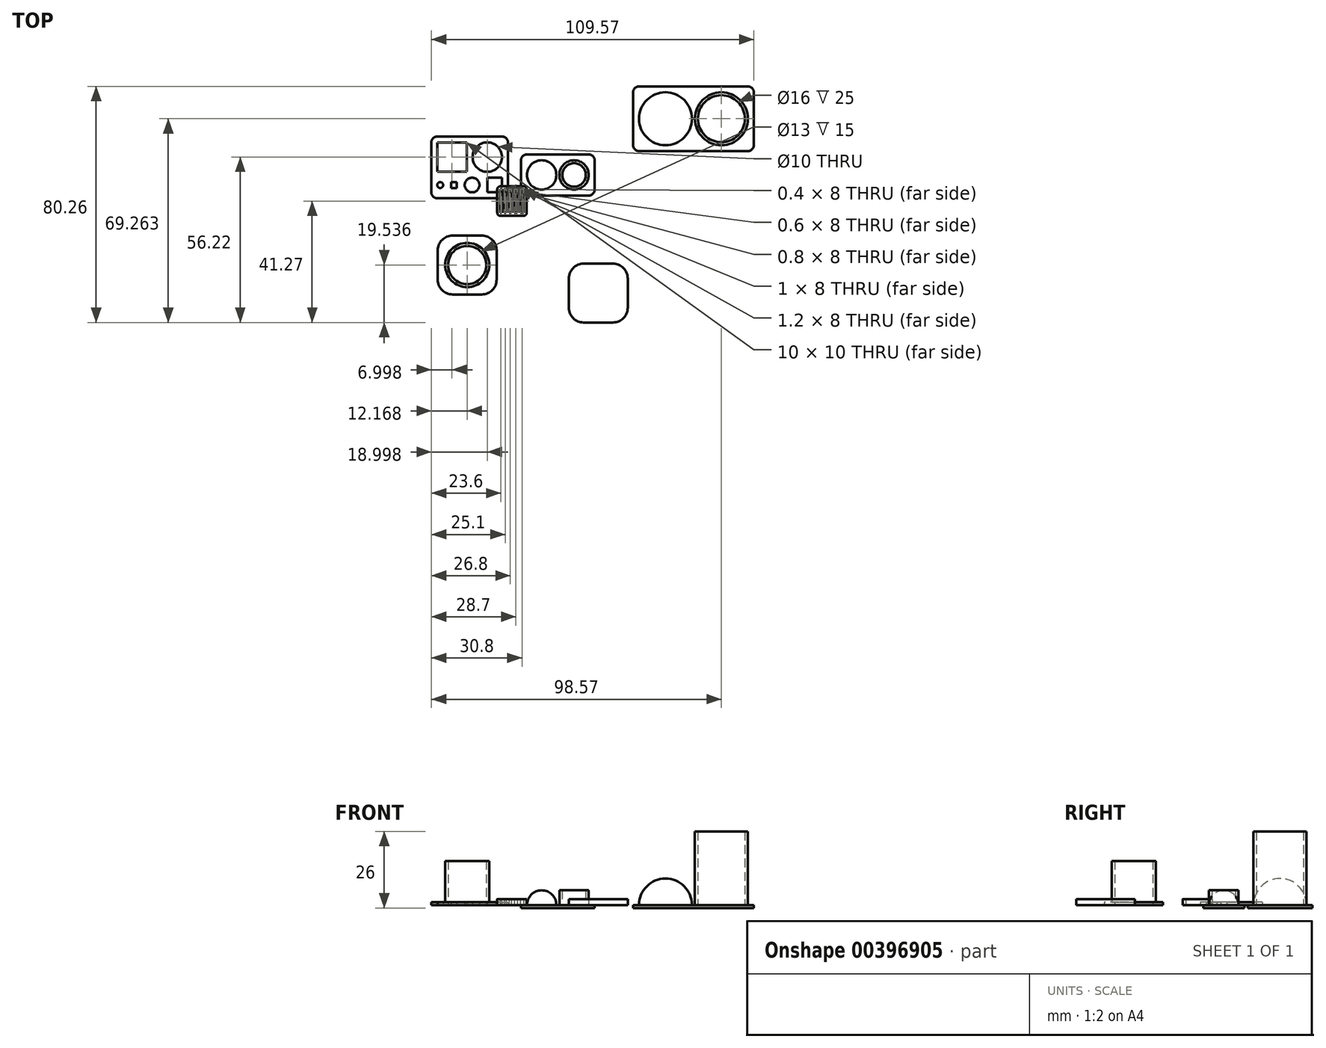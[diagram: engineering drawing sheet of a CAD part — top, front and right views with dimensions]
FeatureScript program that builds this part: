
annotation { "Feature Type Name" : "Feature", "Feature Type Description" : "" }
export const myFeature = defineFeature(function(context is Context, id is Id, definition is map)
    precondition{}
    {
        {
            var Q0;
            Q0=qCreatedBy(makeId("Top.planeOp"),FACE);
            var sketch = newSketch(context, id + "F0", { "sketchPlane" : qUnion([Q0])});
            skCircle(sketch, "E0", {"center": v(21.09, 8.88) * mm, "radius": 4 * mm});
            skCircle(sketch, "E1.0", {"center": v(21.09, 8.88) * mm, "radius": 5 * mm});
            skLineSegment(sketch, "E2", {"start": v(5.09, 8.88) * mm, "end": v(15.09, 8.88) * mm});
            skArc(sketch, "E3", {"start": v(15.09, 8.88) * mm, "mid": v(10.09, 13.88) * mm, "end": v(5.09, 8.88) * mm});
            skLineSegment(sketch, "E4.bottom", {"start": v(5.09, 15.88) * mm, "end": v(26.09, 15.88) * mm});
            skLineSegment(sketch, "E4.top", {"start": v(5.09, 1.88) * mm, "end": v(26.09, 1.88) * mm});
            skLineSegment(sketch, "E4.left", {"start": v(3.09, 13.88) * mm, "end": v(3.09, 3.88) * mm});
            skLineSegment(sketch, "E4.right", {"start": v(28.09, 13.88) * mm, "end": v(28.09, 3.88) * mm});
            skLineSegment(sketch, "E5", {"start": v(5.09, 8.88) * mm, "end": v(5.09, 15.88) * mm, "construction": true});
            skLineSegment(sketch, "E6", {"start": v(5.09, 8.88) * mm, "end": v(5.09, 1.88) * mm, "construction": true});
            skArc(sketch, "E7", {"start": v(5.09, 8.88) * mm, "mid": v(10.09, 3.88) * mm, "end": v(15.09, 8.88) * mm});
            skPoint(sketch, "E8.visualSharp", {"position": v(3.09, 15.88) * mm});
            skArc(sketch, "E8.filletArc", {"start": v(5.09, 15.88) * mm, "mid": v(3.67, 15.3) * mm, "end": v(3.09, 13.88) * mm});
            skPoint(sketch, "E9.visualSharp", {"position": v(3.09, 1.88) * mm});
            skArc(sketch, "E9.filletArc", {"start": v(3.09, 3.88) * mm, "mid": v(3.67, 2.46) * mm, "end": v(5.09, 1.88) * mm});
            skPoint(sketch, "E10.visualSharp", {"position": v(28.09, 1.88) * mm});
            skArc(sketch, "E10.filletArc", {"start": v(26.09, 1.88) * mm, "mid": v(27.5, 2.46) * mm, "end": v(28.09, 3.88) * mm});
            skPoint(sketch, "E11.visualSharp", {"position": v(28.09, 15.88) * mm});
            skArc(sketch, "E11.filletArc", {"start": v(28.09, 13.88) * mm, "mid": v(27.5, 15.3) * mm, "end": v(26.09, 15.88) * mm});
            skCircle(sketch, "E12", {"center": v(71.17, 28) * mm, "radius": 8 * mm});
            skCircle(sketch, "E13.0", {"center": v(71.17, 28) * mm, "radius": 9 * mm});
            skLineSegment(sketch, "E14", {"start": v(43.17, 28) * mm, "end": v(61.17, 28) * mm});
            skArc(sketch, "E15", {"start": v(61.17, 28) * mm, "mid": v(52.17, 37) * mm, "end": v(43.17, 28) * mm});
            skLineSegment(sketch, "E16.bottom", {"start": v(43.17, 39) * mm, "end": v(80.17, 39) * mm});
            skLineSegment(sketch, "E16.top", {"start": v(43.17, 17) * mm, "end": v(80.17, 17) * mm});
            skLineSegment(sketch, "E16.left", {"start": v(41.17, 37) * mm, "end": v(41.17, 19) * mm});
            skLineSegment(sketch, "E16.right", {"start": v(82.17, 37) * mm, "end": v(82.17, 19) * mm});
            skLineSegment(sketch, "E17", {"start": v(43.17, 28) * mm, "end": v(43.17, 39) * mm, "construction": true});
            skLineSegment(sketch, "E18", {"start": v(43.17, 28) * mm, "end": v(43.17, 17) * mm, "construction": true});
            skArc(sketch, "E19", {"start": v(43.17, 28) * mm, "mid": v(52.17, 19) * mm, "end": v(61.17, 28) * mm});
            skPoint(sketch, "E20.visualSharp", {"position": v(41.17, 39) * mm});
            skArc(sketch, "E20.filletArc", {"start": v(43.17, 39) * mm, "mid": v(41.76, 38.4) * mm, "end": v(41.17, 37) * mm});
            skPoint(sketch, "E21.visualSharp", {"position": v(41.17, 17) * mm});
            skArc(sketch, "E21.filletArc", {"start": v(41.17, 19) * mm, "mid": v(41.76, 17.58) * mm, "end": v(43.17, 17) * mm});
            skPoint(sketch, "E22.visualSharp", {"position": v(82.17, 17) * mm});
            skArc(sketch, "E22.filletArc", {"start": v(80.17, 17) * mm, "mid": v(81.58, 17.58) * mm, "end": v(82.17, 19) * mm});
            skPoint(sketch, "E23.visualSharp", {"position": v(82.17, 39) * mm});
            skArc(sketch, "E23.filletArc", {"start": v(82.17, 37) * mm, "mid": v(81.58, 38.4) * mm, "end": v(80.17, 39) * mm});
            skSolve(sketch);
        }
        {
            var Q0;
            Q0=makeQuery(id+"F0.imprint","IMPRINT",FACE,{"disambiguationData":[TD([[makeQuery(id+"F0.imprint","IMPRINT",EDGE,{"derivedFrom":sQuery(id+"F0.wireOp",EDGE,"E1.0")}),-1.0]])]});
            var Q1;
            Q1=makeQuery(id+"F0.imprint","IMPRINT",FACE,{"disambiguationData":[TD([[makeQuery(id+"F0.imprint","IMPRINT",EDGE,{"derivedFrom":sQuery(id+"F0.wireOp",EDGE,"E0")}),1.0]])]});
            var Q2;
            Q2=makeQuery(id+"F0.imprint","IMPRINT",FACE,{"disambiguationData":[TD([[makeQuery(id+"F0.imprint","IMPRINT",EDGE,{"derivedFrom":sQuery(id+"F0.wireOp",EDGE,"E0")}),-1.0]])]});
            var Q3;
            Q3=makeQuery(id+"F0.imprint","IMPRINT",FACE,{"disambiguationData":[TD([[makeQuery(id+"F0.imprint","IMPRINT",EDGE,{"derivedFrom":sQuery(id+"F0.wireOp",EDGE,"E2")}),-1.0]])]});
            var Q4;
            Q4=makeQuery(id+"F0.imprint","IMPRINT",FACE,{"disambiguationData":[TD([[makeQuery(id+"F0.imprint","IMPRINT",EDGE,{"derivedFrom":sQuery(id+"F0.wireOp",EDGE,"E2")}),1.0]])]});
            var Q5;
            Q5=makeQuery(id+"F0.imprint","IMPRINT",FACE,{"disambiguationData":[TD([[makeQuery(id+"F0.imprint","IMPRINT",EDGE,{"derivedFrom":sQuery(id+"F0.wireOp",EDGE,"E13.0")}),-1.0]])]});
            var Q6;
            Q6=makeQuery(id+"F0.imprint","IMPRINT",FACE,{"disambiguationData":[TD([[makeQuery(id+"F0.imprint","IMPRINT",EDGE,{"derivedFrom":sQuery(id+"F0.wireOp",EDGE,"E14")}),-1.0]])]});
            var Q7;
            Q7=makeQuery(id+"F0.imprint","IMPRINT",FACE,{"disambiguationData":[TD([[makeQuery(id+"F0.imprint","IMPRINT",EDGE,{"derivedFrom":sQuery(id+"F0.wireOp",EDGE,"E14")}),1.0]])]});
            var Q8;
            Q8=makeQuery(id+"F0.imprint","IMPRINT",FACE,{"disambiguationData":[TD([[makeQuery(id+"F0.imprint","IMPRINT",EDGE,{"derivedFrom":sQuery(id+"F0.wireOp",EDGE,"E12")}),-1.0]])]});
            var Q9;
            Q9=makeQuery(id+"F0.imprint","IMPRINT",FACE,{"disambiguationData":[TD([[makeQuery(id+"F0.imprint","IMPRINT",EDGE,{"derivedFrom":sQuery(id+"F0.wireOp",EDGE,"E12")}),1.0]])]});
            extrude(context, id + "F1", {"entities" : qUnion([Q0, Q1, Q2, Q3, Q4, Q5, Q6, Q7, Q8, Q9]), "oppositeDirection" : true, "depth" : 1 * mm, "offsetDistance" : 25 * mm});
        }
        {
            var Q0;
            Q0=makeQuery(id+"F0.imprint","IMPRINT",FACE,{"disambiguationData":[TD([[makeQuery(id+"F0.imprint","IMPRINT",EDGE,{"derivedFrom":sQuery(id+"F0.wireOp",EDGE,"E2")}),1.0]])]});
            var Q1;
            Q1=sQuery(id+"F0.wireOp",EDGE,"E2");
            revolve(context, id + "F2", {"operationType" : NewBodyOperationType.ADD, "entities" : qUnion([Q0]), "axis" : qUnion([Q1]), "revolveType" : RevolveType.ONE_DIRECTION, "angle" : 180 * degree});
        }
        {
            var Q0;
            Q0=makeQuery(id+"F0.imprint","IMPRINT",FACE,{"disambiguationData":[TD([[makeQuery(id+"F0.imprint","IMPRINT",EDGE,{"derivedFrom":sQuery(id+"F0.wireOp",EDGE,"E0")}),-1.0]])]});
            extrude(context, id + "F3", {"entities" : qUnion([Q0]), "operationType" : NewBodyOperationType.ADD, "depth" : 5 * mm});
        }
        {
            var Q0;
            Q0=qCreatedBy(makeId("Top.planeOp"),FACE);
            var sketch = newSketch(context, id + "F4", { "sketchPlane" : qUnion([Q0])});
            skLineSegment(sketch, "E24.bottom", {"start": v(-15.4, 9.95) * mm, "end": v(-25.4, 9.95) * mm});
            skLineSegment(sketch, "E24.top", {"start": v(-15.4, 19.95) * mm, "end": v(-25.4, 19.95) * mm});
            skLineSegment(sketch, "E24.left", {"start": v(-15.4, 9.95) * mm, "end": v(-15.4, 19.95) * mm});
            skLineSegment(sketch, "E24.right", {"start": v(-25.4, 9.95) * mm, "end": v(-25.4, 19.95) * mm});
            skPoint(sketch, "E24.middle", {"position": v(-20.4, 14.95) * mm});
            skLineSegment(sketch, "E25.bottom", {"start": v(-3.4, 2.95) * mm, "end": v(-8.4, 2.95) * mm});
            skLineSegment(sketch, "E25.top", {"start": v(-3.4, 7.95) * mm, "end": v(-8.4, 7.95) * mm});
            skLineSegment(sketch, "E25.left", {"start": v(-8.4, 2.95) * mm, "end": v(-8.4, 7.95) * mm});
            skLineSegment(sketch, "E25.right", {"start": v(-3.4, 2.95) * mm, "end": v(-3.4, 7.95) * mm});
            skPoint(sketch, "E25.middle", {"position": v(-5.9, 5.45) * mm});
            skLineSegment(sketch, "E26.bottom", {"start": v(-18.74, 4.45) * mm, "end": v(-20.74, 4.45) * mm});
            skLineSegment(sketch, "E26.top", {"start": v(-18.74, 6.45) * mm, "end": v(-20.74, 6.45) * mm});
            skLineSegment(sketch, "E26.left", {"start": v(-18.74, 4.45) * mm, "end": v(-18.74, 6.45) * mm});
            skLineSegment(sketch, "E26.right", {"start": v(-20.74, 4.45) * mm, "end": v(-20.74, 6.45) * mm});
            skPoint(sketch, "E26.middle", {"position": v(-19.74, 5.45) * mm});
            skCircle(sketch, "E27", {"center": v(-8.4, 14.95) * mm, "radius": 5 * mm});
            skCircle(sketch, "E28", {"center": v(-13.57, 5.45) * mm, "radius": 2.5 * mm});
            skCircle(sketch, "E29", {"center": v(-24.4, 5.45) * mm, "radius": 1 * mm});
            skPoint(sketch, "E30", {"position": v(-5.9, 2.95) * mm});
            skLineSegment(sketch, "E31", {"start": v(-23.4, 5.45) * mm, "end": v(-20.74, 5.45) * mm, "construction": true});
            skLineSegment(sketch, "E32", {"start": v(-18.74, 5.45) * mm, "end": v(-16.07, 5.45) * mm, "construction": true});
            skLineSegment(sketch, "E33", {"start": v(-15.4, 14.95) * mm, "end": v(-13.4, 14.95) * mm, "construction": true});
            skLineSegment(sketch, "E34", {"start": v(-25.4, 9.95) * mm, "end": v(-25.4, -1.2) * mm, "construction": true});
            skLineSegment(sketch, "E35", {"start": v(-3.4, 7.95) * mm, "end": v(-3.4, 22.63) * mm, "construction": true});
            skLineSegment(sketch, "E36", {"start": v(-8.4, 9.95) * mm, "end": v(-8.4, 7.95) * mm, "construction": true});
            skLineSegment(sketch, "E37", {"start": v(-8.4, 5.45) * mm, "end": v(-11.07, 5.45) * mm, "construction": true});
            skLineSegment(sketch, "E38.bottom", {"start": v(-25.4, 21.95) * mm, "end": v(-3.4, 21.95) * mm});
            skLineSegment(sketch, "E38.top", {"start": v(-25.4, 0.95) * mm, "end": v(-3.4, 0.95) * mm});
            skLineSegment(sketch, "E38.left", {"start": v(-27.4, 19.95) * mm, "end": v(-27.4, 2.95) * mm});
            skLineSegment(sketch, "E38.right", {"start": v(-1.4, 19.95) * mm, "end": v(-1.4, 2.95) * mm});
            skPoint(sketch, "E39.visualSharp", {"position": v(-1.4, 21.95) * mm});
            skArc(sketch, "E39.filletArc", {"start": v(-1.4, 19.95) * mm, "mid": v(-1.99, 21.36) * mm, "end": v(-3.4, 21.95) * mm});
            skPoint(sketch, "E40.visualSharp", {"position": v(-27.4, 21.95) * mm});
            skArc(sketch, "E40.filletArc", {"start": v(-25.4, 21.95) * mm, "mid": v(-26.82, 21.36) * mm, "end": v(-27.4, 19.95) * mm});
            skPoint(sketch, "E41.visualSharp", {"position": v(-27.4, 0.95) * mm});
            skArc(sketch, "E41.filletArc", {"start": v(-27.4, 2.95) * mm, "mid": v(-26.82, 1.54) * mm, "end": v(-25.4, 0.95) * mm});
            skPoint(sketch, "E42.visualSharp", {"position": v(-1.4, 0.95) * mm});
            skArc(sketch, "E42.filletArc", {"start": v(-3.4, 0.95) * mm, "mid": v(-1.99, 1.54) * mm, "end": v(-1.4, 2.95) * mm});
            skSolve(sketch);
        }
        {
            var Q0;
            Q0=makeQuery(id+"F4.imprint","IMPRINT",FACE,{"disambiguationData":[TD([[makeQuery(id+"F4.imprint","IMPRINT",EDGE,{"derivedFrom":sQuery(id+"F4.wireOp",EDGE,"E24.bottom")}),1.0]])]});
            extrude(context, id + "F5", {"entities" : qUnion([Q0]), "depth" : 1 * mm, "offsetDistance" : 25 * mm});
        }
        {
            var Q0;
            Q0=qCreatedBy(makeId("Top.planeOp"),FACE);
            var sketch = newSketch(context, id + "F6", { "sketchPlane" : qUnion([Q0])});
            skLineSegment(sketch, "E43.bottom", {"start": v(4, -4) * mm, "end": v(-4, -4) * mm});
            skLineSegment(sketch, "E43.top", {"start": v(4, 4) * mm, "end": v(-4, 4) * mm});
            skLineSegment(sketch, "E43.left", {"start": v(4, -4) * mm, "end": v(4, 4) * mm});
            skLineSegment(sketch, "E43.right", {"start": v(-4, -4) * mm, "end": v(-4, 4) * mm});
            skPoint(sketch, "E43.middle", {"position": v(0, 0) * mm});
            skLineSegment(sketch, "E44.0", {"start": v(4, 5) * mm, "end": v(-4, 5) * mm});
            skLineSegment(sketch, "E44.1", {"start": v(5, -4) * mm, "end": v(5, 4) * mm});
            skLineSegment(sketch, "E44.2", {"start": v(4, -5) * mm, "end": v(-4, -5) * mm});
            skLineSegment(sketch, "E44.3", {"start": v(-5, -4) * mm, "end": v(-5, 4) * mm});
            skLineSegment(sketch, "E45.bottom", {"start": v(-3.6, 4) * mm, "end": v(-2.6, 4) * mm});
            skLineSegment(sketch, "E45.top", {"start": v(-3.6, -4) * mm, "end": v(-2.6, -4) * mm});
            skLineSegment(sketch, "E45.left", {"start": v(-3.6, 4) * mm, "end": v(-3.6, -4) * mm});
            skLineSegment(sketch, "E45.right", {"start": v(-2.6, 4) * mm, "end": v(-2.6, -4) * mm});
            skLineSegment(sketch, "E46.bottom", {"start": v(-2, 4) * mm, "end": v(-1, 4) * mm});
            skLineSegment(sketch, "E46.top", {"start": v(-2, -4) * mm, "end": v(-1, -4) * mm});
            skLineSegment(sketch, "E46.left", {"start": v(-2, 4) * mm, "end": v(-2, -4) * mm});
            skLineSegment(sketch, "E46.right", {"start": v(-1, 4) * mm, "end": v(-1, -4) * mm});
            skLineSegment(sketch, "E47.bottom", {"start": v(-0.2, 4) * mm, "end": v(0.8, 4) * mm});
            skLineSegment(sketch, "E47.top", {"start": v(-0.2, -4) * mm, "end": v(0.8, -4) * mm});
            skLineSegment(sketch, "E47.left", {"start": v(-0.2, 4) * mm, "end": v(-0.2, -4) * mm});
            skLineSegment(sketch, "E47.right", {"start": v(0.8, 4) * mm, "end": v(0.8, -4) * mm});
            skLineSegment(sketch, "E48.bottom", {"start": v(1.8, 4) * mm, "end": v(2.8, 4) * mm});
            skLineSegment(sketch, "E48.top", {"start": v(1.8, -4) * mm, "end": v(2.8, -4) * mm});
            skLineSegment(sketch, "E48.left", {"start": v(1.8, 4) * mm, "end": v(1.8, -4) * mm});
            skLineSegment(sketch, "E48.right", {"start": v(2.8, 4) * mm, "end": v(2.8, -4) * mm});
            skPoint(sketch, "E49.visualSharp", {"position": v(-5, 5) * mm});
            skArc(sketch, "E49.filletArc", {"start": v(-4, 5) * mm, "mid": v(-4.7, 4.7) * mm, "end": v(-5, 4) * mm});
            skPoint(sketch, "E50.visualSharp", {"position": v(-5, -5) * mm});
            skArc(sketch, "E50.filletArc", {"start": v(-5, -4) * mm, "mid": v(-4.7, -4.7) * mm, "end": v(-4, -5) * mm});
            skPoint(sketch, "E51.visualSharp", {"position": v(5, -5) * mm});
            skArc(sketch, "E51.filletArc", {"start": v(4, -5) * mm, "mid": v(4.7, -4.7) * mm, "end": v(5, -4) * mm});
            skPoint(sketch, "E52.visualSharp", {"position": v(5, 5) * mm});
            skArc(sketch, "E52.filletArc", {"start": v(5, 4) * mm, "mid": v(4.7, 4.7) * mm, "end": v(4, 5) * mm});
            skSolve(sketch);
        }
        {
            var Q0;
            {var subQ1=sQuery(id+"F6.wireOp",EDGE,"E43.left");Q0=makeQuery(id+"F6.imprint","IMPRINT",FACE,{"disambiguationData":[TD([[makeQuery(id+"F6.imprint","IMPRINT",EDGE,{"derivedFrom":subQ1}),-1.0]])]});}
            var Q1;
            {var subQ0=sQuery(id+"F6.wireOp",EDGE,"E45.left");Q1=makeQuery(id+"F6.imprint","IMPRINT",FACE,{"disambiguationData":[TD([[makeQuery(id+"F6.imprint","IMPRINT",EDGE,{"derivedFrom":subQ0}),1.0]])]});}
            var Q2;
            {var subQ0=sQuery(id+"F6.wireOp",EDGE,"E46.left");Q2=makeQuery(id+"F6.imprint","IMPRINT",FACE,{"disambiguationData":[TD([[makeQuery(id+"F6.imprint","IMPRINT",EDGE,{"derivedFrom":subQ0}),1.0]])]});}
            var Q3;
            {var subQ0=sQuery(id+"F6.wireOp",EDGE,"E47.left");Q3=makeQuery(id+"F6.imprint","IMPRINT",FACE,{"disambiguationData":[TD([[makeQuery(id+"F6.imprint","IMPRINT",EDGE,{"derivedFrom":subQ0}),1.0]])]});}
            var Q4;
            {var subQ0=sQuery(id+"F6.wireOp",EDGE,"E48.left");Q4=makeQuery(id+"F6.imprint","IMPRINT",FACE,{"disambiguationData":[TD([[makeQuery(id+"F6.imprint","IMPRINT",EDGE,{"derivedFrom":subQ0}),1.0]])]});}
            extrude(context, id + "F7", {"entities" : qUnion([Q0, Q1, Q2, Q3, Q4]), "depth" : 2 * mm, "offsetDistance" : 25 * mm});
        }
        {
            var Q0;
            Q0=makeQuery(id+"F0.imprint","IMPRINT",FACE,{"disambiguationData":[TD([[makeQuery(id+"F0.imprint","IMPRINT",EDGE,{"derivedFrom":sQuery(id+"F0.wireOp",EDGE,"E14")}),1.0]])]});
            var Q1;
            Q1=sQuery(id+"F0.wireOp",EDGE,"E14");
            revolve(context, id + "F8", {"operationType" : NewBodyOperationType.ADD, "entities" : qUnion([Q0]), "axis" : qUnion([Q1]), "revolveType" : RevolveType.ONE_DIRECTION, "angle" : 180 * degree});
        }
        {
            var Q0;
            Q0=makeQuery(id+"F0.imprint","IMPRINT",FACE,{"disambiguationData":[TD([[makeQuery(id+"F0.imprint","IMPRINT",EDGE,{"derivedFrom":sQuery(id+"F0.wireOp",EDGE,"E12")}),-1.0]])]});
            extrude(context, id + "F9", {"entities" : qUnion([Q0]), "operationType" : NewBodyOperationType.ADD, "depth" : 25 * mm, "offsetDistance" : 25 * mm});
        }
        {
            var Q0;
            Q0=qCreatedBy(makeId("Top.planeOp"),FACE);
            var sketch = newSketch(context, id + "F10", { "sketchPlane" : qUnion([Q0])});
            skCircle(sketch, "E53", {"center": v(-15.23, -21.73) * mm, "radius": 7.5 * mm});
            skLineSegment(sketch, "E54.bottom", {"start": v(-10.23, -31.73) * mm, "end": v(-20.23, -31.73) * mm});
            skLineSegment(sketch, "E54.top", {"start": v(-10.23, -11.73) * mm, "end": v(-20.23, -11.73) * mm});
            skLineSegment(sketch, "E54.left", {"start": v(-5.23, -26.73) * mm, "end": v(-5.23, -16.73) * mm});
            skLineSegment(sketch, "E54.right", {"start": v(-25.23, -26.73) * mm, "end": v(-25.23, -16.73) * mm});
            skPoint(sketch, "E55.visualSharp", {"position": v(-25.23, -11.73) * mm});
            skArc(sketch, "E55.filletArc", {"start": v(-20.23, -11.73) * mm, "mid": v(-23.77, -13.2) * mm, "end": v(-25.23, -16.73) * mm});
            skPoint(sketch, "E56.visualSharp", {"position": v(-5.23, -11.73) * mm});
            skArc(sketch, "E56.filletArc", {"start": v(-5.23, -16.73) * mm, "mid": v(-6.7, -13.2) * mm, "end": v(-10.23, -11.73) * mm});
            skPoint(sketch, "E57.visualSharp", {"position": v(-5.23, -31.73) * mm});
            skArc(sketch, "E57.filletArc", {"start": v(-10.23, -31.73) * mm, "mid": v(-6.7, -30.27) * mm, "end": v(-5.23, -26.73) * mm});
            skPoint(sketch, "E58.visualSharp", {"position": v(-25.23, -31.73) * mm});
            skArc(sketch, "E58.filletArc", {"start": v(-25.23, -26.73) * mm, "mid": v(-23.77, -30.27) * mm, "end": v(-20.23, -31.73) * mm});
            skCircle(sketch, "E59", {"center": v(-15.23, -21.73) * mm, "radius": 6.5 * mm});
            skSolve(sketch);
        }
        {
            var Q0;
            Q0=makeQuery(id+"F10.imprint","IMPRINT",FACE,{"disambiguationData":[TD([[makeQuery(id+"F10.imprint","IMPRINT",EDGE,{"derivedFrom":sQuery(id+"F10.wireOp",EDGE,"E53")}),-1.0]])]});
            extrude(context, id + "F11", {"entities" : qUnion([Q0]), "depth" : 1 * mm, "offsetDistance" : 25 * mm});
        }
        {
            var Q0;
            Q0=makeQuery(id+"F10.imprint","IMPRINT",FACE,{"disambiguationData":[TD([[makeQuery(id+"F10.imprint","IMPRINT",EDGE,{"derivedFrom":sQuery(id+"F10.wireOp",EDGE,"E53")}),1.0]])]});
            extrude(context, id + "F12", {"entities" : qUnion([Q0]), "operationType" : NewBodyOperationType.ADD, "depth" : 15 * mm, "offsetDistance" : 25 * mm});
        }
        {
            var Q0;
            Q0=qCreatedBy(makeId("Top.planeOp"),FACE);
            var sketch = newSketch(context, id + "F13", { "sketchPlane" : qUnion([Q0])});
            skLineSegment(sketch, "E60.bottom", {"start": v(24.32, -21.27) * mm, "end": v(34.32, -21.27) * mm});
            skLineSegment(sketch, "E60.top", {"start": v(24.32, -41.27) * mm, "end": v(34.32, -41.27) * mm});
            skLineSegment(sketch, "E60.left", {"start": v(19.32, -26.27) * mm, "end": v(19.32, -36.27) * mm});
            skLineSegment(sketch, "E60.right", {"start": v(39.32, -26.27) * mm, "end": v(39.32, -36.27) * mm});
            skPoint(sketch, "E61.visualSharp", {"position": v(39.32, -21.27) * mm});
            skArc(sketch, "E61.filletArc", {"start": v(39.32, -26.27) * mm, "mid": v(37.86, -22.74) * mm, "end": v(34.32, -21.27) * mm});
            skPoint(sketch, "E62.visualSharp", {"position": v(19.32, -21.27) * mm});
            skArc(sketch, "E62.filletArc", {"start": v(24.32, -21.27) * mm, "mid": v(20.79, -22.74) * mm, "end": v(19.32, -26.27) * mm});
            skPoint(sketch, "E63.visualSharp", {"position": v(19.32, -41.27) * mm});
            skArc(sketch, "E63.filletArc", {"start": v(19.32, -36.27) * mm, "mid": v(20.79, -39.8) * mm, "end": v(24.32, -41.27) * mm});
            skPoint(sketch, "E64.visualSharp", {"position": v(39.32, -41.27) * mm});
            skArc(sketch, "E64.filletArc", {"start": v(34.32, -41.27) * mm, "mid": v(37.86, -39.8) * mm, "end": v(39.32, -36.27) * mm});
            skSolve(sketch);
        }
        {
            var Q0;
            Q0=makeQuery(id+"F13.imprint","IMPRINT",FACE,{"disambiguationData":[TD([[makeQuery(id+"F13.imprint","IMPRINT",EDGE,{"derivedFrom":sQuery(id+"F13.wireOp",EDGE,"E60.bottom")}),-1.0]])]});
            extrude(context, id + "F14", {"entities" : qUnion([Q0]), "depth" : 2 * mm, "offsetDistance" : 25 * mm});
        }
    });
